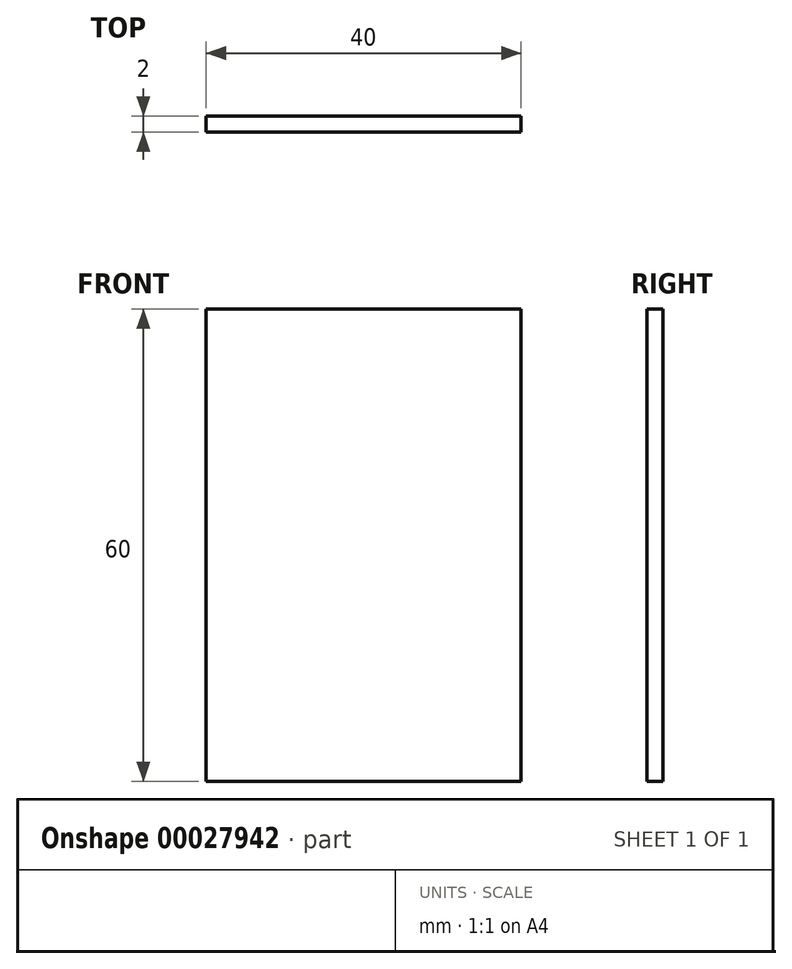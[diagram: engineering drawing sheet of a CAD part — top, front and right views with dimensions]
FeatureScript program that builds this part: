
annotation { "Feature Type Name" : "Feature", "Feature Type Description" : "" }
export const myFeature = defineFeature(function(context is Context, id is Id, definition is map)
    precondition{}
    {
        {
            var Q0;
            Q0=qCreatedBy(makeId("Front.planeOp"),FACE);
            var sketch = newSketch(context, id + "F0", { "sketchPlane" : qUnion([Q0])});
            skLineSegment(sketch, "E0.bottom", {"start": v(0, 0) * mm, "end": v(40, 0) * mm});
            skLineSegment(sketch, "E0.top", {"start": v(0, 60) * mm, "end": v(40, 60) * mm});
            skLineSegment(sketch, "E0.left", {"start": v(0, 0) * mm, "end": v(0, 60) * mm});
            skLineSegment(sketch, "E0.right", {"start": v(40, 0) * mm, "end": v(40, 60) * mm});
            skLineSegment(sketch, "E1", {"start": v(0, 60) * mm, "end": v(0, 59) * mm});
            skSolve(sketch);
        }
        {
            var Q0;
            Q0=makeQuery(id+"F0.imprint","IMPRINT",FACE,{"disambiguationData":[TD([[makeQuery(id+"F0.imprint","IMPRINT",EDGE,{"derivedFrom":sQuery(id+"F0.wireOp",EDGE,"E0.bottom")}),1.0]])]});
            extrude(context, id + "F1", {"entities" : qUnion([Q0]), "depth" : 2 * mm});
        }
    });
